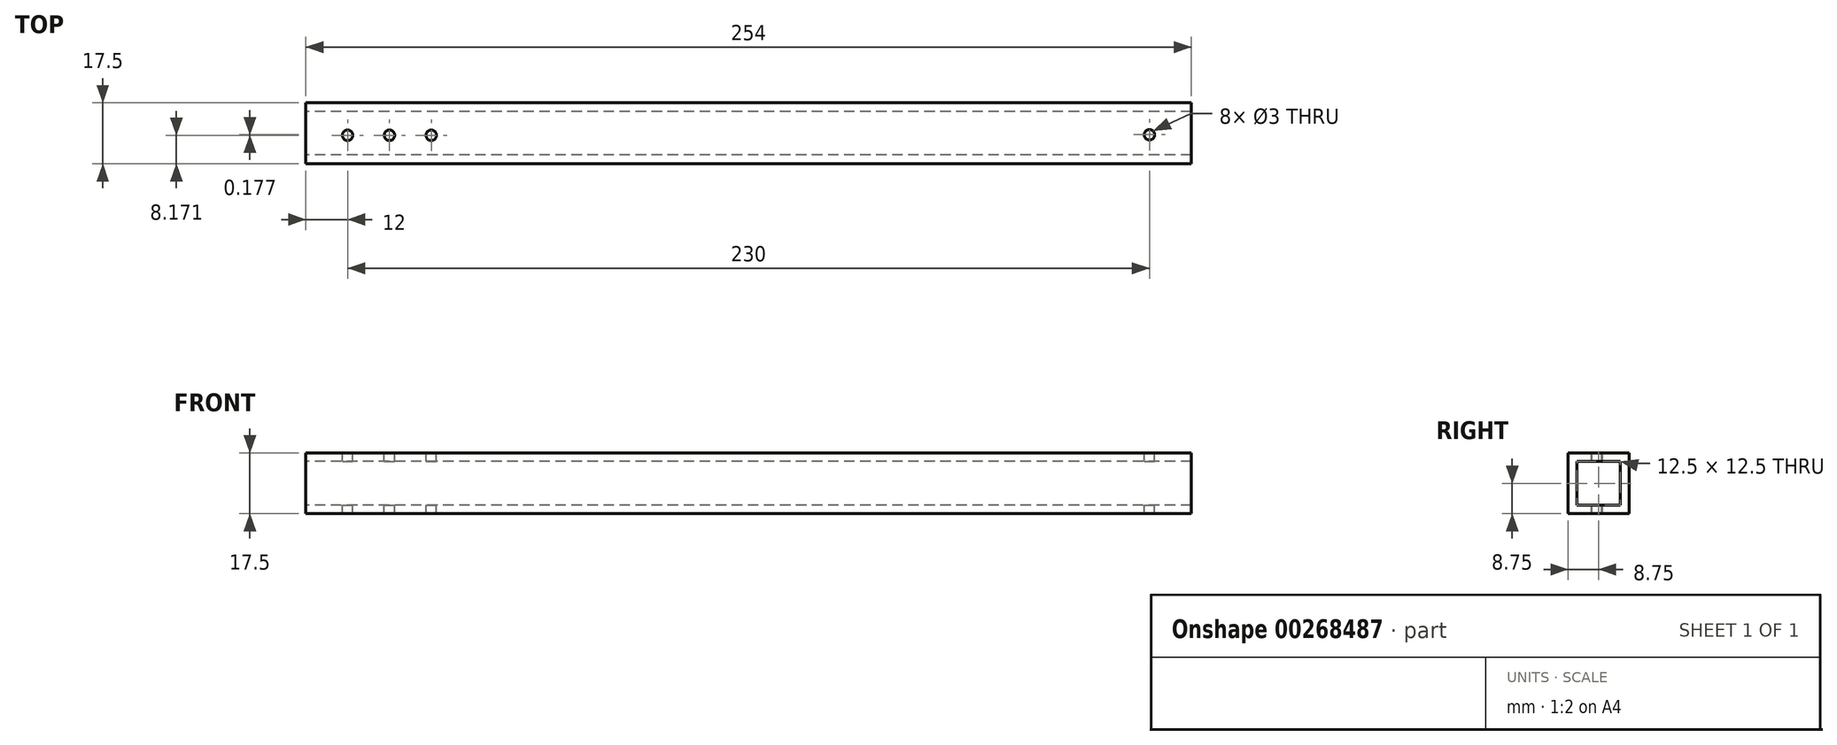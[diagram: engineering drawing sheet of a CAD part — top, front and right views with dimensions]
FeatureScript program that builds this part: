
annotation { "Feature Type Name" : "Feature", "Feature Type Description" : "" }
export const myFeature = defineFeature(function(context is Context, id is Id, definition is map)
    precondition{}
    {
        {
            var Q0;
            Q0=qCreatedBy(makeId("Right.planeOp"),FACE);
            var sketch = newSketch(context, id + "F0", { "sketchPlane" : qUnion([Q0])});
            skLineSegment(sketch, "E0.bottom", {"start": v(0, 0) * mm, "end": v(-12.5, 0) * mm});
            skLineSegment(sketch, "E0.top", {"start": v(0, 12.5) * mm, "end": v(-12.5, 12.5) * mm});
            skLineSegment(sketch, "E0.left", {"start": v(0, 0) * mm, "end": v(0, 12.5) * mm});
            skLineSegment(sketch, "E0.right", {"start": v(-12.5, 0) * mm, "end": v(-12.5, 12.5) * mm});
            skLineSegment(sketch, "E1.0", {"start": v(2.5, -2.5) * mm, "end": v(2.5, 15) * mm});
            skLineSegment(sketch, "E1.1", {"start": v(2.5, -2.5) * mm, "end": v(-15, -2.5) * mm});
            skLineSegment(sketch, "E1.2", {"start": v(-15, -2.5) * mm, "end": v(-15, 15) * mm});
            skLineSegment(sketch, "E1.3", {"start": v(2.5, 15) * mm, "end": v(-15, 15) * mm});
            skSolve(sketch);
        }
        {
            var Q0;
            Q0=makeQuery(id+"F0.imprint","IMPRINT",FACE,{"disambiguationData":[TD([[makeQuery(id+"F0.imprint","IMPRINT",EDGE,{"derivedFrom":sQuery(id+"F0.wireOp",EDGE,"E0.bottom")}),1.0]])]});
            extrude(context, id + "F1", {"entities" : qUnion([Q0]), "depth" : 254 * mm});
        }
        {
            var Q0;
            Q0=makeQuery(id+"F1.opExtrude","SWEPT_FACE",FACE,{"disambiguationData":[OSD([sQuery(id+"F0.wireOp",EDGE,"E1.3")])]});
            var sketch = newSketch(context, id + "F2", { "sketchPlane" : qUnion([Q0])});
            skPoint(sketch, "E2", {"position": v(12, -6.83) * mm});
            skPoint(sketch, "E3", {"position": v(24, -6.83) * mm});
            skPoint(sketch, "E4", {"position": v(36, -6.83) * mm});
            skPoint(sketch, "E5", {"position": v(242, -6.65) * mm});
            skPoint(sketch, "E6", {"position": v(254, -6.65) * mm});
            skSolve(sketch);
        }
        {
            var Q0;
            Q0=sQuery(id+"F2.wireOp",VERTEX,"E2");
            var Q1;
            Q1=sQuery(id+"F2.wireOp",VERTEX,"E3");
            var Q2;
            Q2=sQuery(id+"F2.wireOp",VERTEX,"E4");
            var Q3;
            Q3=sQuery(id+"F2.wireOp",VERTEX,"E5");
            var Q4;
            Q4=makeQuery(id+"F1.opExtrude","SWEPT_BODY",BODY,{"disambiguationData":[OSD([sQuery(id+"F0.wireOp",EDGE,"E0.bottom"),sQuery(id+"F0.wireOp",EDGE,"E0.top"),sQuery(id+"F0.wireOp",EDGE,"E0.left"),sQuery(id+"F0.wireOp",EDGE,"E0.right"),sQuery(id+"F0.wireOp",EDGE,"E1.0"),sQuery(id+"F0.wireOp",EDGE,"E1.1"),sQuery(id+"F0.wireOp",EDGE,"E1.2"),sQuery(id+"F0.wireOp",EDGE,"E1.3")])]});
            hole(context, id + "F3", {"style" : HoleStyle.SIMPLE, "endStyle" : HoleEndStyle.THROUGH, "holeDiameter" : 3 * mm, "tappedDepth" : 12 * mm, "tapClearance" : 3, "locations" : qUnion([Q0, Q1, Q2, Q3]), "scope" : qUnion([Q4])});
        }
    });
